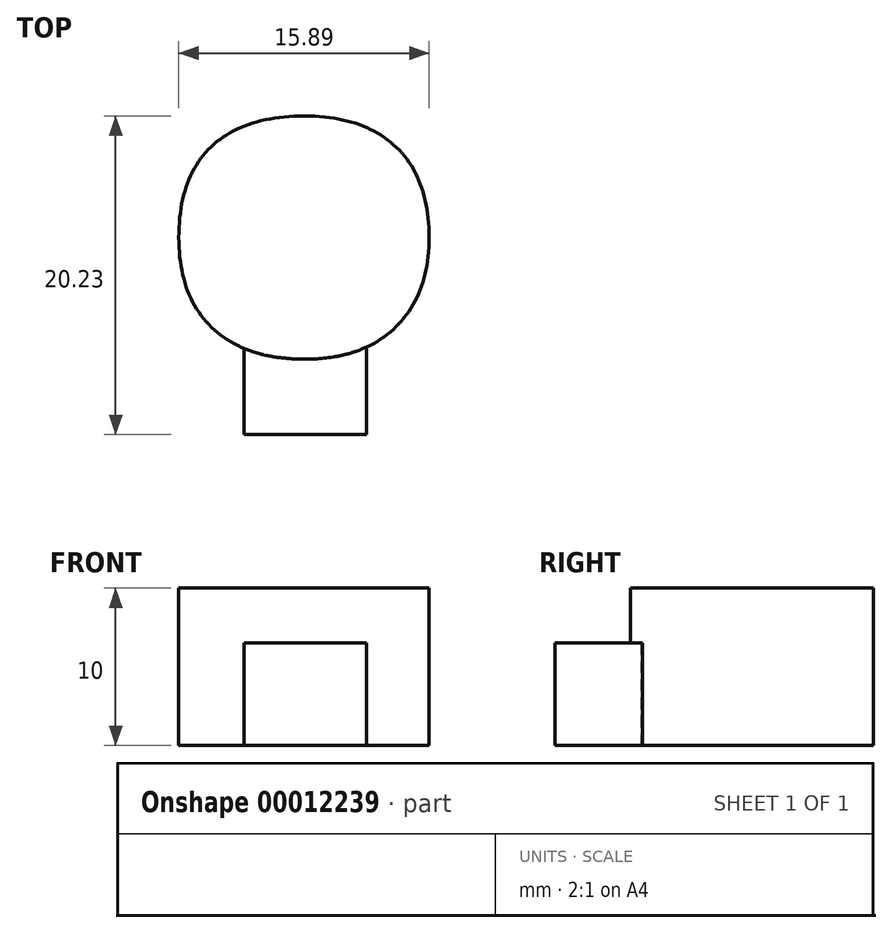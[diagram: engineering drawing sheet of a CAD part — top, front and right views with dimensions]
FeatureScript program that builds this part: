
annotation { "Feature Type Name" : "Feature", "Feature Type Description" : "" }
export const myFeature = defineFeature(function(context is Context, id is Id, definition is map)
    precondition{}
    {
        {
            var Q0;
            Q0=qCreatedBy(makeId("Top.planeOp"),FACE);
            var sketch = newSketch(context, id + "F0", { "sketchPlane" : qUnion([Q0])});
            skText(sketch, "E0", { "text": ".", "fontName": "OpenSans-Bold.ttf"});
            const initialGuessF0  = {"E0": [-0.02725, 0, 1, 0, 0.067]};
            skSetInitialGuess(sketch, initialGuessF0);
            skSolve(sketch);
        }
        {
            var Q0;
            Q0=makeQuery(id+"F0.imprint","IMPRINT",FACE,{"disambiguationData":[TD([[makeQuery(id+"F0.imprint","IMPRINT",EDGE,{"derivedFrom":sQuery(id+"F0.wireOp",EDGE,"E0.sketch_text.stroke-0")}),-1.0]])]});
            extrude(context, id + "F1", {"entities" : qUnion([Q0]), "depth" : 10 * mm});
        }
        {
            var Q0;
            Q0=qCreatedBy(makeId("Top.planeOp"),FACE);
            var sketch = newSketch(context, id + "F2", { "sketchPlane" : qUnion([Q0])});
            skLineSegment(sketch, "E1.bottom", {"start": v(-17.8, 1.29) * mm, "end": v(-10, 1.29) * mm});
            skLineSegment(sketch, "E1.top", {"start": v(-17.8, -6) * mm, "end": v(-10, -6) * mm});
            skLineSegment(sketch, "E1.left", {"start": v(-17.8, 1.29) * mm, "end": v(-17.8, -6) * mm});
            skLineSegment(sketch, "E1.right", {"start": v(-10, 1.29) * mm, "end": v(-10, -6) * mm});
            skSolve(sketch);
        }
        {
            var Q0;
            Q0 = qSketchRegion(id + "F2", true);
            extrude(context, id + "F3", {"entities" : qUnion([Q0]), "operationType" : NewBodyOperationType.ADD, "depth" : 6.5 * mm});
        }
    });
